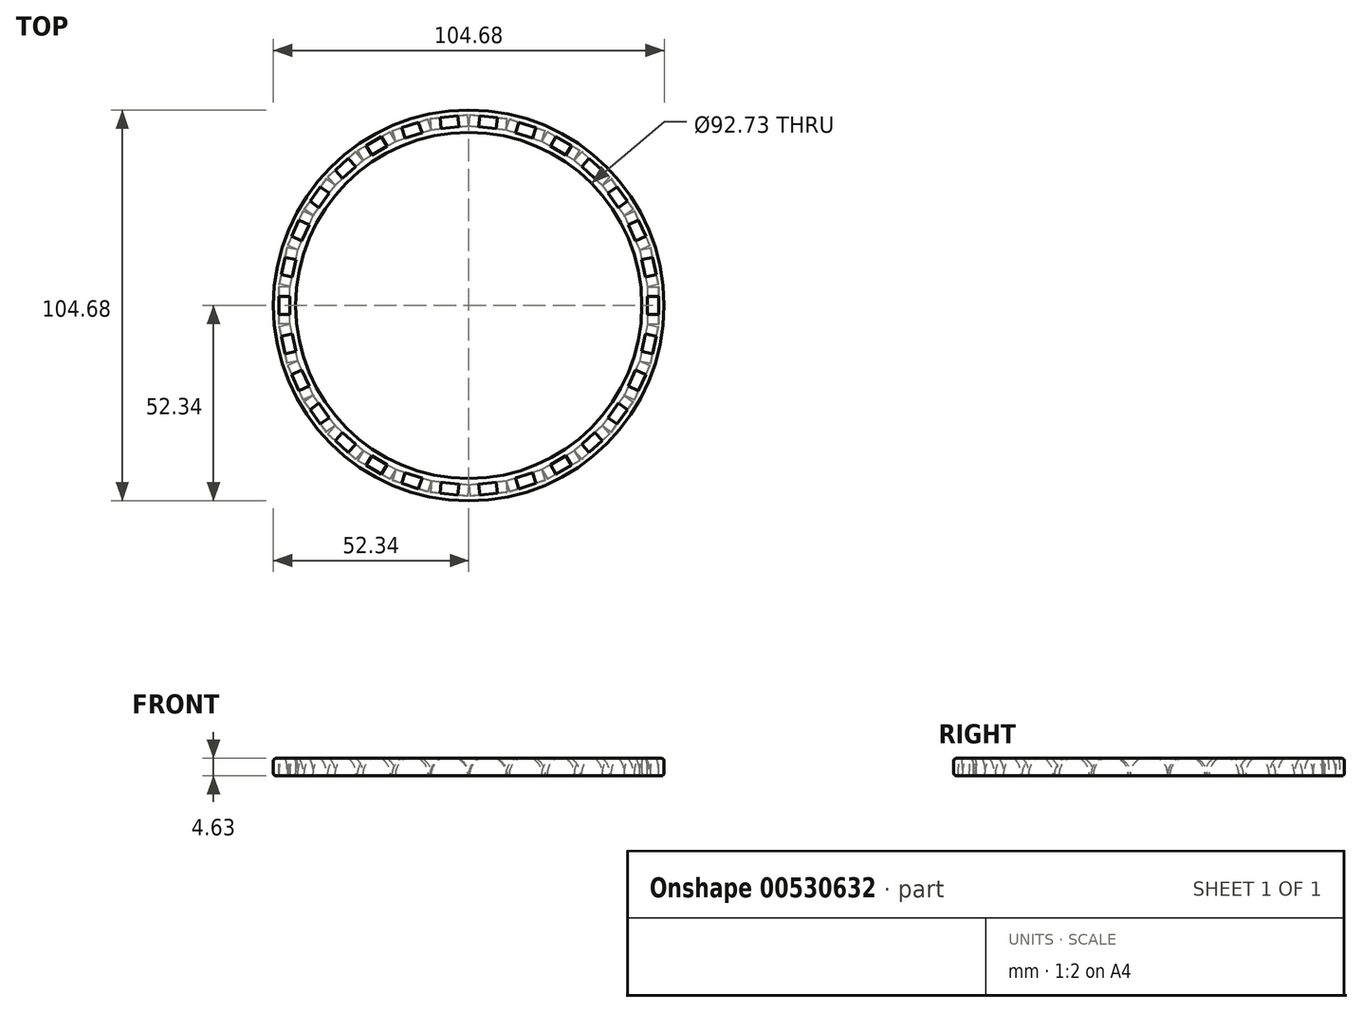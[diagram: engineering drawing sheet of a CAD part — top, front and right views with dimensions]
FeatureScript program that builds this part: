
annotation { "Feature Type Name" : "Feature", "Feature Type Description" : "" }
export const myFeature = defineFeature(function(context is Context, id is Id, definition is map)
    precondition{}
    {
        {
            var Q0;
            Q0=qCreatedBy(makeId("Front.planeOp"),FACE);
            var sketch = newSketch(context, id + "F0", { "sketchPlane" : qUnion([Q0])});
            skLineSegment(sketch, "E0", {"start": v(0, 0) * mm, "end": v(0, 19.8) * mm});
            skLineSegment(sketch, "E1", {"start": v(-50.84, 0) * mm, "end": v(-50.84, 10) * mm});
            skLineSegment(sketch, "E2", {"start": v(-50.84, 10) * mm, "end": v(-47.87, 10) * mm});
            skLineSegment(sketch, "E3", {"start": v(-47.87, 10) * mm, "end": v(-47.87, 0) * mm});
            skLineSegment(sketch, "E4", {"start": v(-47.87, 0) * mm, "end": v(-50.84, 0) * mm});
            skLineSegment(sketch, "E5", {"start": v(-50.84, 5) * mm, "end": v(-47.87, 5) * mm});
            skLineSegment(sketch, "E6", {"start": v(-50.84, 4.77) * mm, "end": v(-52.34, 4.77) * mm});
            skLineSegment(sketch, "E7", {"start": v(-52.34, 4.77) * mm, "end": v(-52.34, 9.4) * mm});
            skLineSegment(sketch, "E8", {"start": v(-52.34, 9.4) * mm, "end": v(-46.37, 9.4) * mm});
            skLineSegment(sketch, "E9", {"start": v(-46.37, 9.4) * mm, "end": v(-46.37, 4.77) * mm});
            skLineSegment(sketch, "E10", {"start": v(-46.37, 4.77) * mm, "end": v(-50.84, 4.77) * mm});
            skPoint(sketch, "E11", {"position": v(-49.35, 0) * mm});
            skSolve(sketch);
        }
        {
            var Q0;
            {var subQ3=sQuery(id+"F0.wireOp",EDGE,"E6");Q0=makeQuery(id+"F0.imprint","IMPRINT",FACE,{"disambiguationData":[TD([[makeQuery(id+"F0.imprint","IMPRINT",EDGE,{"derivedFrom":subQ3}),-1.0]])]});}
            var Q1;
            {var subQ0=sQuery(id+"F0.wireOp",EDGE,"E5");Q1=makeQuery(id+"F0.imprint","IMPRINT",FACE,{"disambiguationData":[TD([[makeQuery(id+"F0.imprint","IMPRINT",EDGE,{"derivedFrom":subQ0}),1.0]])]});}
            var Q2;
            {var subQ0=sQuery(id+"F0.wireOp",EDGE,"E9");Q2=makeQuery(id+"F0.imprint","IMPRINT",FACE,{"disambiguationData":[TD([[makeQuery(id+"F0.imprint","IMPRINT",EDGE,{"derivedFrom":subQ0}),-1.0]])]});}
            var Q3;
            {var subQ0=sQuery(id+"F0.wireOp",EDGE,"E5");Q3=makeQuery(id+"F0.imprint","IMPRINT",FACE,{"disambiguationData":[TD([[makeQuery(id+"F0.imprint","IMPRINT",EDGE,{"derivedFrom":subQ0}),-1.0]])]});}
            var Q4;
            Q4=sQuery(id+"F0.wireOp",EDGE,"E0");
            revolve(context, id + "F1", {"entities" : qUnion([Q0, Q1, Q2, Q3]), "axis" : qUnion([Q4]), "revolveType" : RevolveType.FULL});
        }
        {
            var Q0;
            {var subQ0=sQuery(id+"F0.wireOp",EDGE,"E4");Q0=makeQuery(id+"F0.imprint","IMPRINT",FACE,{"disambiguationData":[TD([[makeQuery(id+"F0.imprint","IMPRINT",EDGE,{"derivedFrom":subQ0}),-1.0]])]});}
            var Q1;
            {var subQ0=sQuery(id+"F0.wireOp",EDGE,"E5");Q1=makeQuery(id+"F0.imprint","IMPRINT",FACE,{"disambiguationData":[TD([[makeQuery(id+"F0.imprint","IMPRINT",EDGE,{"derivedFrom":subQ0}),-1.0]])]});}
            var Q2;
            Q2=sQuery(id+"F0.wireOp",EDGE,"E5");
            revolve(context, id + "F2", {"entities" : qUnion([Q0, Q1]), "axis" : qUnion([Q2]), "revolveType" : RevolveType.FULL});
        }
        {
            var Q0;
            Q0=makeQuery(id+"F2.opRevolve","SWEPT_BODY",BODY,{"disambiguationData":[OSD([sQuery(id+"F0.wireOp",EDGE,"E1"),sQuery(id+"F0.wireOp",EDGE,"E3"),sQuery(id+"F0.wireOp",EDGE,"E4"),sQuery(id+"F0.wireOp",EDGE,"E5")])]});
            var Q1;
            Q1=sQuery(id+"F0.wireOp",EDGE,"E0");
            circularPattern(context, id + "F3", {"operationType" : NewBodyOperationType.REMOVE, "entities" : qUnion([Q0]), "axis" : qUnion([Q1]), "angle" : 360 * degree, "instanceCount" : 30, "equalSpace" : true});
        }
        {
            var Q0;
            Q0=makeQuery(id+"F1.opRevolve","SWEPT_EDGE",EDGE,{"disambiguationData":[OSD([sQuery(id+"F0.wireOp",EDGE,"E6"),sQuery(id+"F0.wireOp",EDGE,"E7")])]});
            var Q1;
            Q1=makeQuery(id+"F1.opRevolve","SWEPT_EDGE",EDGE,{"disambiguationData":[OSD([sQuery(id+"F0.wireOp",EDGE,"E9"),sQuery(id+"F0.wireOp",EDGE,"E10")])]});
            var Q2;
            Q2=makeQuery(id+"F1.opRevolve","SWEPT_EDGE",EDGE,{"disambiguationData":[OSD([sQuery(id+"F0.wireOp",EDGE,"E7"),sQuery(id+"F0.wireOp",EDGE,"E8")])]});
            var Q3;
            Q3=makeQuery(id+"F1.opRevolve","SWEPT_EDGE",EDGE,{"disambiguationData":[OSD([sQuery(id+"F0.wireOp",EDGE,"E8"),sQuery(id+"F0.wireOp",EDGE,"E9")])]});
            fillet(context, id + "F4", {"entities" : qUnion([Q0, Q1, Q2, Q3]), "radius" : 0.7 * mm, "tangentPropagation" : true, "allowEdgeOverflow" : false});
        }
        {
            var Q0;
            Q0=makeQuery(id+"F3.boolean.opBoolean","INTERSECT",EDGE,{"derivedFrom":[makeQuery(id+"F1.opRevolve","SWEPT_FACE",FACE,{"disambiguationData":[OSD([sQuery(id+"F0.wireOp",EDGE,"E6"),sQuery(id+"F0.wireOp",EDGE,"E10")])]}),makeQuery(id+"F3.opPattern","COPY",FACE,{"derivedFrom":makeQuery(id+"F2.opRevolve","SWEPT_FACE",FACE,{"disambiguationData":[OSD([sQuery(id+"F0.wireOp",EDGE,"E3")])]}),"instanceName":"21"})]});
            var Q1;
            Q1=makeQuery(id+"F3.boolean.opBoolean","INTERSECT",EDGE,{"derivedFrom":[makeQuery(id+"F1.opRevolve","SWEPT_FACE",FACE,{"disambiguationData":[OSD([sQuery(id+"F0.wireOp",EDGE,"E6"),sQuery(id+"F0.wireOp",EDGE,"E10")])]}),makeQuery(id+"F3.opPattern","COPY",FACE,{"derivedFrom":makeQuery(id+"F2.opRevolve","SWEPT_FACE",FACE,{"disambiguationData":[OSD([sQuery(id+"F0.wireOp",EDGE,"E1")])]}),"instanceName":"21"})]});
            var Q2;
            Q2=makeQuery(id+"F3.boolean.opBoolean","INTERSECT",EDGE,{"derivedFrom":[makeQuery(id+"F1.opRevolve","SWEPT_FACE",FACE,{"disambiguationData":[OSD([sQuery(id+"F0.wireOp",EDGE,"E6"),sQuery(id+"F0.wireOp",EDGE,"E10")])]}),makeQuery(id+"F3.opPattern","COPY",FACE,{"derivedFrom":makeQuery(id+"F2.opRevolve","SWEPT_FACE",FACE,{"disambiguationData":[OSD([sQuery(id+"F0.wireOp",EDGE,"E1")])]}),"instanceName":"22"})]});
            var Q3;
            Q3=makeQuery(id+"F3.boolean.opBoolean","INTERSECT",EDGE,{"derivedFrom":[makeQuery(id+"F1.opRevolve","SWEPT_FACE",FACE,{"disambiguationData":[OSD([sQuery(id+"F0.wireOp",EDGE,"E6"),sQuery(id+"F0.wireOp",EDGE,"E10")])]}),makeQuery(id+"F3.opPattern","COPY",FACE,{"derivedFrom":makeQuery(id+"F2.opRevolve","SWEPT_FACE",FACE,{"disambiguationData":[OSD([sQuery(id+"F0.wireOp",EDGE,"E3")])]}),"instanceName":"22"})]});
            var Q4;
            Q4=makeQuery(id+"F3.boolean.opBoolean","INTERSECT",EDGE,{"derivedFrom":[makeQuery(id+"F1.opRevolve","SWEPT_FACE",FACE,{"disambiguationData":[OSD([sQuery(id+"F0.wireOp",EDGE,"E6"),sQuery(id+"F0.wireOp",EDGE,"E10")])]}),makeQuery(id+"F3.opPattern","COPY",FACE,{"derivedFrom":makeQuery(id+"F2.opRevolve","SWEPT_FACE",FACE,{"disambiguationData":[OSD([sQuery(id+"F0.wireOp",EDGE,"E3")])]}),"instanceName":"23"})]});
            var Q5;
            Q5=makeQuery(id+"F3.boolean.opBoolean","INTERSECT",EDGE,{"derivedFrom":[makeQuery(id+"F1.opRevolve","SWEPT_FACE",FACE,{"disambiguationData":[OSD([sQuery(id+"F0.wireOp",EDGE,"E6"),sQuery(id+"F0.wireOp",EDGE,"E10")])]}),makeQuery(id+"F3.opPattern","COPY",FACE,{"derivedFrom":makeQuery(id+"F2.opRevolve","SWEPT_FACE",FACE,{"disambiguationData":[OSD([sQuery(id+"F0.wireOp",EDGE,"E1")])]}),"instanceName":"23"})]});
            var Q6;
            Q6=makeQuery(id+"F3.boolean.opBoolean","INTERSECT",EDGE,{"derivedFrom":[makeQuery(id+"F1.opRevolve","SWEPT_FACE",FACE,{"disambiguationData":[OSD([sQuery(id+"F0.wireOp",EDGE,"E6"),sQuery(id+"F0.wireOp",EDGE,"E10")])]}),makeQuery(id+"F3.opPattern","COPY",FACE,{"derivedFrom":makeQuery(id+"F2.opRevolve","SWEPT_FACE",FACE,{"disambiguationData":[OSD([sQuery(id+"F0.wireOp",EDGE,"E1")])]}),"instanceName":"24"})]});
            var Q7;
            Q7=makeQuery(id+"F3.boolean.opBoolean","INTERSECT",EDGE,{"derivedFrom":[makeQuery(id+"F1.opRevolve","SWEPT_FACE",FACE,{"disambiguationData":[OSD([sQuery(id+"F0.wireOp",EDGE,"E6"),sQuery(id+"F0.wireOp",EDGE,"E10")])]}),makeQuery(id+"F3.opPattern","COPY",FACE,{"derivedFrom":makeQuery(id+"F2.opRevolve","SWEPT_FACE",FACE,{"disambiguationData":[OSD([sQuery(id+"F0.wireOp",EDGE,"E3")])]}),"instanceName":"24"})]});
            var Q8;
            Q8=makeQuery(id+"F3.boolean.opBoolean","INTERSECT",EDGE,{"derivedFrom":[makeQuery(id+"F1.opRevolve","SWEPT_FACE",FACE,{"disambiguationData":[OSD([sQuery(id+"F0.wireOp",EDGE,"E6"),sQuery(id+"F0.wireOp",EDGE,"E10")])]}),makeQuery(id+"F3.opPattern","COPY",FACE,{"derivedFrom":makeQuery(id+"F2.opRevolve","SWEPT_FACE",FACE,{"disambiguationData":[OSD([sQuery(id+"F0.wireOp",EDGE,"E3")])]}),"instanceName":"25"})]});
            var Q9;
            Q9=makeQuery(id+"F3.boolean.opBoolean","INTERSECT",EDGE,{"derivedFrom":[makeQuery(id+"F1.opRevolve","SWEPT_FACE",FACE,{"disambiguationData":[OSD([sQuery(id+"F0.wireOp",EDGE,"E6"),sQuery(id+"F0.wireOp",EDGE,"E10")])]}),makeQuery(id+"F3.opPattern","COPY",FACE,{"derivedFrom":makeQuery(id+"F2.opRevolve","SWEPT_FACE",FACE,{"disambiguationData":[OSD([sQuery(id+"F0.wireOp",EDGE,"E1")])]}),"instanceName":"25"})]});
            var Q10;
            Q10=makeQuery(id+"F3.boolean.opBoolean","INTERSECT",EDGE,{"derivedFrom":[makeQuery(id+"F1.opRevolve","SWEPT_FACE",FACE,{"disambiguationData":[OSD([sQuery(id+"F0.wireOp",EDGE,"E6"),sQuery(id+"F0.wireOp",EDGE,"E10")])]}),makeQuery(id+"F3.opPattern","COPY",FACE,{"derivedFrom":makeQuery(id+"F2.opRevolve","SWEPT_FACE",FACE,{"disambiguationData":[OSD([sQuery(id+"F0.wireOp",EDGE,"E1")])]}),"instanceName":"26"})]});
            var Q11;
            Q11=makeQuery(id+"F3.boolean.opBoolean","INTERSECT",EDGE,{"derivedFrom":[makeQuery(id+"F1.opRevolve","SWEPT_FACE",FACE,{"disambiguationData":[OSD([sQuery(id+"F0.wireOp",EDGE,"E6"),sQuery(id+"F0.wireOp",EDGE,"E10")])]}),makeQuery(id+"F3.opPattern","COPY",FACE,{"derivedFrom":makeQuery(id+"F2.opRevolve","SWEPT_FACE",FACE,{"disambiguationData":[OSD([sQuery(id+"F0.wireOp",EDGE,"E3")])]}),"instanceName":"26"})]});
            var Q12;
            Q12=makeQuery(id+"F3.boolean.opBoolean","INTERSECT",EDGE,{"derivedFrom":[makeQuery(id+"F1.opRevolve","SWEPT_FACE",FACE,{"disambiguationData":[OSD([sQuery(id+"F0.wireOp",EDGE,"E6"),sQuery(id+"F0.wireOp",EDGE,"E10")])]}),makeQuery(id+"F3.opPattern","COPY",FACE,{"derivedFrom":makeQuery(id+"F2.opRevolve","SWEPT_FACE",FACE,{"disambiguationData":[OSD([sQuery(id+"F0.wireOp",EDGE,"E3")])]}),"instanceName":"27"})]});
            var Q13;
            Q13=makeQuery(id+"F3.boolean.opBoolean","INTERSECT",EDGE,{"derivedFrom":[makeQuery(id+"F1.opRevolve","SWEPT_FACE",FACE,{"disambiguationData":[OSD([sQuery(id+"F0.wireOp",EDGE,"E6"),sQuery(id+"F0.wireOp",EDGE,"E10")])]}),makeQuery(id+"F3.opPattern","COPY",FACE,{"derivedFrom":makeQuery(id+"F2.opRevolve","SWEPT_FACE",FACE,{"disambiguationData":[OSD([sQuery(id+"F0.wireOp",EDGE,"E1")])]}),"instanceName":"27"})]});
            var Q14;
            Q14=makeQuery(id+"F3.boolean.opBoolean","INTERSECT",EDGE,{"derivedFrom":[makeQuery(id+"F1.opRevolve","SWEPT_FACE",FACE,{"disambiguationData":[OSD([sQuery(id+"F0.wireOp",EDGE,"E6"),sQuery(id+"F0.wireOp",EDGE,"E10")])]}),makeQuery(id+"F3.opPattern","COPY",FACE,{"derivedFrom":makeQuery(id+"F2.opRevolve","SWEPT_FACE",FACE,{"disambiguationData":[OSD([sQuery(id+"F0.wireOp",EDGE,"E1")])]}),"instanceName":"28"})]});
            var Q15;
            Q15=makeQuery(id+"F3.boolean.opBoolean","INTERSECT",EDGE,{"derivedFrom":[makeQuery(id+"F1.opRevolve","SWEPT_FACE",FACE,{"disambiguationData":[OSD([sQuery(id+"F0.wireOp",EDGE,"E6"),sQuery(id+"F0.wireOp",EDGE,"E10")])]}),makeQuery(id+"F3.opPattern","COPY",FACE,{"derivedFrom":makeQuery(id+"F2.opRevolve","SWEPT_FACE",FACE,{"disambiguationData":[OSD([sQuery(id+"F0.wireOp",EDGE,"E3")])]}),"instanceName":"28"})]});
            var Q16;
            Q16=makeQuery(id+"F3.boolean.opBoolean","INTERSECT",EDGE,{"derivedFrom":[makeQuery(id+"F1.opRevolve","SWEPT_FACE",FACE,{"disambiguationData":[OSD([sQuery(id+"F0.wireOp",EDGE,"E6"),sQuery(id+"F0.wireOp",EDGE,"E10")])]}),makeQuery(id+"F2.opRevolve","SWEPT_FACE",FACE,{"disambiguationData":[OSD([sQuery(id+"F0.wireOp",EDGE,"E1")])]})]});
            var Q17;
            Q17=makeQuery(id+"F3.boolean.opBoolean","INTERSECT",EDGE,{"derivedFrom":[makeQuery(id+"F1.opRevolve","SWEPT_FACE",FACE,{"disambiguationData":[OSD([sQuery(id+"F0.wireOp",EDGE,"E6"),sQuery(id+"F0.wireOp",EDGE,"E10")])]}),makeQuery(id+"F2.opRevolve","SWEPT_FACE",FACE,{"disambiguationData":[OSD([sQuery(id+"F0.wireOp",EDGE,"E3")])]})]});
            var Q18;
            Q18=makeQuery(id+"F3.boolean.opBoolean","INTERSECT",EDGE,{"derivedFrom":[makeQuery(id+"F1.opRevolve","SWEPT_FACE",FACE,{"disambiguationData":[OSD([sQuery(id+"F0.wireOp",EDGE,"E6"),sQuery(id+"F0.wireOp",EDGE,"E10")])]}),makeQuery(id+"F3.opPattern","COPY",FACE,{"derivedFrom":makeQuery(id+"F2.opRevolve","SWEPT_FACE",FACE,{"disambiguationData":[OSD([sQuery(id+"F0.wireOp",EDGE,"E3")])]}),"instanceName":"1"})]});
            var Q19;
            Q19=makeQuery(id+"F3.boolean.opBoolean","INTERSECT",EDGE,{"derivedFrom":[makeQuery(id+"F1.opRevolve","SWEPT_FACE",FACE,{"disambiguationData":[OSD([sQuery(id+"F0.wireOp",EDGE,"E6"),sQuery(id+"F0.wireOp",EDGE,"E10")])]}),makeQuery(id+"F3.opPattern","COPY",FACE,{"derivedFrom":makeQuery(id+"F2.opRevolve","SWEPT_FACE",FACE,{"disambiguationData":[OSD([sQuery(id+"F0.wireOp",EDGE,"E1")])]}),"instanceName":"1"})]});
            var Q20;
            Q20=makeQuery(id+"F3.boolean.opBoolean","INTERSECT",EDGE,{"derivedFrom":[makeQuery(id+"F1.opRevolve","SWEPT_FACE",FACE,{"disambiguationData":[OSD([sQuery(id+"F0.wireOp",EDGE,"E6"),sQuery(id+"F0.wireOp",EDGE,"E10")])]}),makeQuery(id+"F3.opPattern","COPY",FACE,{"derivedFrom":makeQuery(id+"F2.opRevolve","SWEPT_FACE",FACE,{"disambiguationData":[OSD([sQuery(id+"F0.wireOp",EDGE,"E3")])]}),"instanceName":"2"})]});
            var Q21;
            Q21=makeQuery(id+"F3.boolean.opBoolean","INTERSECT",EDGE,{"derivedFrom":[makeQuery(id+"F1.opRevolve","SWEPT_FACE",FACE,{"disambiguationData":[OSD([sQuery(id+"F0.wireOp",EDGE,"E6"),sQuery(id+"F0.wireOp",EDGE,"E10")])]}),makeQuery(id+"F3.opPattern","COPY",FACE,{"derivedFrom":makeQuery(id+"F2.opRevolve","SWEPT_FACE",FACE,{"disambiguationData":[OSD([sQuery(id+"F0.wireOp",EDGE,"E1")])]}),"instanceName":"2"})]});
            var Q22;
            Q22=makeQuery(id+"F3.boolean.opBoolean","INTERSECT",EDGE,{"derivedFrom":[makeQuery(id+"F1.opRevolve","SWEPT_FACE",FACE,{"disambiguationData":[OSD([sQuery(id+"F0.wireOp",EDGE,"E6"),sQuery(id+"F0.wireOp",EDGE,"E10")])]}),makeQuery(id+"F3.opPattern","COPY",FACE,{"derivedFrom":makeQuery(id+"F2.opRevolve","SWEPT_FACE",FACE,{"disambiguationData":[OSD([sQuery(id+"F0.wireOp",EDGE,"E1")])]}),"instanceName":"3"})]});
            var Q23;
            Q23=makeQuery(id+"F3.boolean.opBoolean","INTERSECT",EDGE,{"derivedFrom":[makeQuery(id+"F1.opRevolve","SWEPT_FACE",FACE,{"disambiguationData":[OSD([sQuery(id+"F0.wireOp",EDGE,"E6"),sQuery(id+"F0.wireOp",EDGE,"E10")])]}),makeQuery(id+"F3.opPattern","COPY",FACE,{"derivedFrom":makeQuery(id+"F2.opRevolve","SWEPT_FACE",FACE,{"disambiguationData":[OSD([sQuery(id+"F0.wireOp",EDGE,"E3")])]}),"instanceName":"3"})]});
            var Q24;
            Q24=makeQuery(id+"F3.boolean.opBoolean","INTERSECT",EDGE,{"derivedFrom":[makeQuery(id+"F1.opRevolve","SWEPT_FACE",FACE,{"disambiguationData":[OSD([sQuery(id+"F0.wireOp",EDGE,"E6"),sQuery(id+"F0.wireOp",EDGE,"E10")])]}),makeQuery(id+"F3.opPattern","COPY",FACE,{"derivedFrom":makeQuery(id+"F2.opRevolve","SWEPT_FACE",FACE,{"disambiguationData":[OSD([sQuery(id+"F0.wireOp",EDGE,"E3")])]}),"instanceName":"4"})]});
            var Q25;
            Q25=makeQuery(id+"F3.boolean.opBoolean","INTERSECT",EDGE,{"derivedFrom":[makeQuery(id+"F1.opRevolve","SWEPT_FACE",FACE,{"disambiguationData":[OSD([sQuery(id+"F0.wireOp",EDGE,"E6"),sQuery(id+"F0.wireOp",EDGE,"E10")])]}),makeQuery(id+"F3.opPattern","COPY",FACE,{"derivedFrom":makeQuery(id+"F2.opRevolve","SWEPT_FACE",FACE,{"disambiguationData":[OSD([sQuery(id+"F0.wireOp",EDGE,"E1")])]}),"instanceName":"4"})]});
            var Q26;
            Q26=makeQuery(id+"F3.boolean.opBoolean","INTERSECT",EDGE,{"derivedFrom":[makeQuery(id+"F1.opRevolve","SWEPT_FACE",FACE,{"disambiguationData":[OSD([sQuery(id+"F0.wireOp",EDGE,"E6"),sQuery(id+"F0.wireOp",EDGE,"E10")])]}),makeQuery(id+"F3.opPattern","COPY",FACE,{"derivedFrom":makeQuery(id+"F2.opRevolve","SWEPT_FACE",FACE,{"disambiguationData":[OSD([sQuery(id+"F0.wireOp",EDGE,"E1")])]}),"instanceName":"5"})]});
            var Q27;
            Q27=makeQuery(id+"F3.boolean.opBoolean","INTERSECT",EDGE,{"derivedFrom":[makeQuery(id+"F1.opRevolve","SWEPT_FACE",FACE,{"disambiguationData":[OSD([sQuery(id+"F0.wireOp",EDGE,"E6"),sQuery(id+"F0.wireOp",EDGE,"E10")])]}),makeQuery(id+"F3.opPattern","COPY",FACE,{"derivedFrom":makeQuery(id+"F2.opRevolve","SWEPT_FACE",FACE,{"disambiguationData":[OSD([sQuery(id+"F0.wireOp",EDGE,"E3")])]}),"instanceName":"5"})]});
            var Q28;
            Q28=makeQuery(id+"F3.boolean.opBoolean","INTERSECT",EDGE,{"derivedFrom":[makeQuery(id+"F1.opRevolve","SWEPT_FACE",FACE,{"disambiguationData":[OSD([sQuery(id+"F0.wireOp",EDGE,"E6"),sQuery(id+"F0.wireOp",EDGE,"E10")])]}),makeQuery(id+"F3.opPattern","COPY",FACE,{"derivedFrom":makeQuery(id+"F2.opRevolve","SWEPT_FACE",FACE,{"disambiguationData":[OSD([sQuery(id+"F0.wireOp",EDGE,"E1")])]}),"instanceName":"7"})]});
            var Q29;
            Q29=makeQuery(id+"F3.boolean.opBoolean","INTERSECT",EDGE,{"derivedFrom":[makeQuery(id+"F1.opRevolve","SWEPT_FACE",FACE,{"disambiguationData":[OSD([sQuery(id+"F0.wireOp",EDGE,"E6"),sQuery(id+"F0.wireOp",EDGE,"E10")])]}),makeQuery(id+"F3.opPattern","COPY",FACE,{"derivedFrom":makeQuery(id+"F2.opRevolve","SWEPT_FACE",FACE,{"disambiguationData":[OSD([sQuery(id+"F0.wireOp",EDGE,"E3")])]}),"instanceName":"7"})]});
            var Q30;
            Q30=makeQuery(id+"F3.boolean.opBoolean","INTERSECT",EDGE,{"derivedFrom":[makeQuery(id+"F1.opRevolve","SWEPT_FACE",FACE,{"disambiguationData":[OSD([sQuery(id+"F0.wireOp",EDGE,"E6"),sQuery(id+"F0.wireOp",EDGE,"E10")])]}),makeQuery(id+"F3.opPattern","COPY",FACE,{"derivedFrom":makeQuery(id+"F2.opRevolve","SWEPT_FACE",FACE,{"disambiguationData":[OSD([sQuery(id+"F0.wireOp",EDGE,"E3")])]}),"instanceName":"6"})]});
            var Q31;
            Q31=makeQuery(id+"F3.boolean.opBoolean","INTERSECT",EDGE,{"derivedFrom":[makeQuery(id+"F1.opRevolve","SWEPT_FACE",FACE,{"disambiguationData":[OSD([sQuery(id+"F0.wireOp",EDGE,"E6"),sQuery(id+"F0.wireOp",EDGE,"E10")])]}),makeQuery(id+"F3.opPattern","COPY",FACE,{"derivedFrom":makeQuery(id+"F2.opRevolve","SWEPT_FACE",FACE,{"disambiguationData":[OSD([sQuery(id+"F0.wireOp",EDGE,"E1")])]}),"instanceName":"6"})]});
            var Q32;
            Q32=makeQuery(id+"F3.boolean.opBoolean","INTERSECT",EDGE,{"derivedFrom":[makeQuery(id+"F1.opRevolve","SWEPT_FACE",FACE,{"disambiguationData":[OSD([sQuery(id+"F0.wireOp",EDGE,"E6"),sQuery(id+"F0.wireOp",EDGE,"E10")])]}),makeQuery(id+"F3.opPattern","COPY",FACE,{"derivedFrom":makeQuery(id+"F2.opRevolve","SWEPT_FACE",FACE,{"disambiguationData":[OSD([sQuery(id+"F0.wireOp",EDGE,"E1")])]}),"instanceName":"8"})]});
            var Q33;
            Q33=makeQuery(id+"F3.boolean.opBoolean","INTERSECT",EDGE,{"derivedFrom":[makeQuery(id+"F1.opRevolve","SWEPT_FACE",FACE,{"disambiguationData":[OSD([sQuery(id+"F0.wireOp",EDGE,"E6"),sQuery(id+"F0.wireOp",EDGE,"E10")])]}),makeQuery(id+"F3.opPattern","COPY",FACE,{"derivedFrom":makeQuery(id+"F2.opRevolve","SWEPT_FACE",FACE,{"disambiguationData":[OSD([sQuery(id+"F0.wireOp",EDGE,"E3")])]}),"instanceName":"8"})]});
            var Q34;
            Q34=makeQuery(id+"F3.boolean.opBoolean","INTERSECT",EDGE,{"derivedFrom":[makeQuery(id+"F1.opRevolve","SWEPT_FACE",FACE,{"disambiguationData":[OSD([sQuery(id+"F0.wireOp",EDGE,"E6"),sQuery(id+"F0.wireOp",EDGE,"E10")])]}),makeQuery(id+"F3.opPattern","COPY",FACE,{"derivedFrom":makeQuery(id+"F2.opRevolve","SWEPT_FACE",FACE,{"disambiguationData":[OSD([sQuery(id+"F0.wireOp",EDGE,"E3")])]}),"instanceName":"9"})]});
            var Q35;
            Q35=makeQuery(id+"F3.boolean.opBoolean","INTERSECT",EDGE,{"derivedFrom":[makeQuery(id+"F1.opRevolve","SWEPT_FACE",FACE,{"disambiguationData":[OSD([sQuery(id+"F0.wireOp",EDGE,"E6"),sQuery(id+"F0.wireOp",EDGE,"E10")])]}),makeQuery(id+"F3.opPattern","COPY",FACE,{"derivedFrom":makeQuery(id+"F2.opRevolve","SWEPT_FACE",FACE,{"disambiguationData":[OSD([sQuery(id+"F0.wireOp",EDGE,"E1")])]}),"instanceName":"9"})]});
            var Q36;
            Q36=makeQuery(id+"F3.boolean.opBoolean","INTERSECT",EDGE,{"derivedFrom":[makeQuery(id+"F1.opRevolve","SWEPT_FACE",FACE,{"disambiguationData":[OSD([sQuery(id+"F0.wireOp",EDGE,"E6"),sQuery(id+"F0.wireOp",EDGE,"E10")])]}),makeQuery(id+"F3.opPattern","COPY",FACE,{"derivedFrom":makeQuery(id+"F2.opRevolve","SWEPT_FACE",FACE,{"disambiguationData":[OSD([sQuery(id+"F0.wireOp",EDGE,"E3")])]}),"instanceName":"10"})]});
            var Q37;
            Q37=makeQuery(id+"F3.boolean.opBoolean","INTERSECT",EDGE,{"derivedFrom":[makeQuery(id+"F1.opRevolve","SWEPT_FACE",FACE,{"disambiguationData":[OSD([sQuery(id+"F0.wireOp",EDGE,"E6"),sQuery(id+"F0.wireOp",EDGE,"E10")])]}),makeQuery(id+"F3.opPattern","COPY",FACE,{"derivedFrom":makeQuery(id+"F2.opRevolve","SWEPT_FACE",FACE,{"disambiguationData":[OSD([sQuery(id+"F0.wireOp",EDGE,"E1")])]}),"instanceName":"10"})]});
            var Q38;
            Q38=makeQuery(id+"F3.boolean.opBoolean","INTERSECT",EDGE,{"derivedFrom":[makeQuery(id+"F1.opRevolve","SWEPT_FACE",FACE,{"disambiguationData":[OSD([sQuery(id+"F0.wireOp",EDGE,"E6"),sQuery(id+"F0.wireOp",EDGE,"E10")])]}),makeQuery(id+"F3.opPattern","COPY",FACE,{"derivedFrom":makeQuery(id+"F2.opRevolve","SWEPT_FACE",FACE,{"disambiguationData":[OSD([sQuery(id+"F0.wireOp",EDGE,"E1")])]}),"instanceName":"11"})]});
            var Q39;
            Q39=makeQuery(id+"F3.boolean.opBoolean","INTERSECT",EDGE,{"derivedFrom":[makeQuery(id+"F1.opRevolve","SWEPT_FACE",FACE,{"disambiguationData":[OSD([sQuery(id+"F0.wireOp",EDGE,"E6"),sQuery(id+"F0.wireOp",EDGE,"E10")])]}),makeQuery(id+"F3.opPattern","COPY",FACE,{"derivedFrom":makeQuery(id+"F2.opRevolve","SWEPT_FACE",FACE,{"disambiguationData":[OSD([sQuery(id+"F0.wireOp",EDGE,"E3")])]}),"instanceName":"11"})]});
            var Q40;
            Q40=makeQuery(id+"F3.boolean.opBoolean","INTERSECT",EDGE,{"derivedFrom":[makeQuery(id+"F1.opRevolve","SWEPT_FACE",FACE,{"disambiguationData":[OSD([sQuery(id+"F0.wireOp",EDGE,"E6"),sQuery(id+"F0.wireOp",EDGE,"E10")])]}),makeQuery(id+"F3.opPattern","COPY",FACE,{"derivedFrom":makeQuery(id+"F2.opRevolve","SWEPT_FACE",FACE,{"disambiguationData":[OSD([sQuery(id+"F0.wireOp",EDGE,"E3")])]}),"instanceName":"12"})]});
            var Q41;
            Q41=makeQuery(id+"F3.boolean.opBoolean","INTERSECT",EDGE,{"derivedFrom":[makeQuery(id+"F1.opRevolve","SWEPT_FACE",FACE,{"disambiguationData":[OSD([sQuery(id+"F0.wireOp",EDGE,"E6"),sQuery(id+"F0.wireOp",EDGE,"E10")])]}),makeQuery(id+"F3.opPattern","COPY",FACE,{"derivedFrom":makeQuery(id+"F2.opRevolve","SWEPT_FACE",FACE,{"disambiguationData":[OSD([sQuery(id+"F0.wireOp",EDGE,"E1")])]}),"instanceName":"13"})]});
            var Q42;
            Q42=makeQuery(id+"F3.boolean.opBoolean","INTERSECT",EDGE,{"derivedFrom":[makeQuery(id+"F1.opRevolve","SWEPT_FACE",FACE,{"disambiguationData":[OSD([sQuery(id+"F0.wireOp",EDGE,"E6"),sQuery(id+"F0.wireOp",EDGE,"E10")])]}),makeQuery(id+"F3.opPattern","COPY",FACE,{"derivedFrom":makeQuery(id+"F2.opRevolve","SWEPT_FACE",FACE,{"disambiguationData":[OSD([sQuery(id+"F0.wireOp",EDGE,"E3")])]}),"instanceName":"13"})]});
            var Q43;
            Q43=makeQuery(id+"F3.boolean.opBoolean","INTERSECT",EDGE,{"derivedFrom":[makeQuery(id+"F1.opRevolve","SWEPT_FACE",FACE,{"disambiguationData":[OSD([sQuery(id+"F0.wireOp",EDGE,"E6"),sQuery(id+"F0.wireOp",EDGE,"E10")])]}),makeQuery(id+"F3.opPattern","COPY",FACE,{"derivedFrom":makeQuery(id+"F2.opRevolve","SWEPT_FACE",FACE,{"disambiguationData":[OSD([sQuery(id+"F0.wireOp",EDGE,"E3")])]}),"instanceName":"14"})]});
            var Q44;
            Q44=makeQuery(id+"F3.boolean.opBoolean","INTERSECT",EDGE,{"derivedFrom":[makeQuery(id+"F1.opRevolve","SWEPT_FACE",FACE,{"disambiguationData":[OSD([sQuery(id+"F0.wireOp",EDGE,"E6"),sQuery(id+"F0.wireOp",EDGE,"E10")])]}),makeQuery(id+"F3.opPattern","COPY",FACE,{"derivedFrom":makeQuery(id+"F2.opRevolve","SWEPT_FACE",FACE,{"disambiguationData":[OSD([sQuery(id+"F0.wireOp",EDGE,"E1")])]}),"instanceName":"14"})]});
            var Q45;
            Q45=makeQuery(id+"F3.boolean.opBoolean","INTERSECT",EDGE,{"derivedFrom":[makeQuery(id+"F1.opRevolve","SWEPT_FACE",FACE,{"disambiguationData":[OSD([sQuery(id+"F0.wireOp",EDGE,"E6"),sQuery(id+"F0.wireOp",EDGE,"E10")])]}),makeQuery(id+"F3.opPattern","COPY",FACE,{"derivedFrom":makeQuery(id+"F2.opRevolve","SWEPT_FACE",FACE,{"disambiguationData":[OSD([sQuery(id+"F0.wireOp",EDGE,"E1")])]}),"instanceName":"12"})]});
            var Q46;
            Q46=makeQuery(id+"F3.boolean.opBoolean","INTERSECT",EDGE,{"derivedFrom":[makeQuery(id+"F1.opRevolve","SWEPT_FACE",FACE,{"disambiguationData":[OSD([sQuery(id+"F0.wireOp",EDGE,"E6"),sQuery(id+"F0.wireOp",EDGE,"E10")])]}),makeQuery(id+"F3.opPattern","COPY",FACE,{"derivedFrom":makeQuery(id+"F2.opRevolve","SWEPT_FACE",FACE,{"disambiguationData":[OSD([sQuery(id+"F0.wireOp",EDGE,"E3")])]}),"instanceName":"15"})]});
            var Q47;
            Q47=makeQuery(id+"F3.boolean.opBoolean","INTERSECT",EDGE,{"derivedFrom":[makeQuery(id+"F1.opRevolve","SWEPT_FACE",FACE,{"disambiguationData":[OSD([sQuery(id+"F0.wireOp",EDGE,"E6"),sQuery(id+"F0.wireOp",EDGE,"E10")])]}),makeQuery(id+"F3.opPattern","COPY",FACE,{"derivedFrom":makeQuery(id+"F2.opRevolve","SWEPT_FACE",FACE,{"disambiguationData":[OSD([sQuery(id+"F0.wireOp",EDGE,"E3")])]}),"instanceName":"16"})]});
            var Q48;
            Q48=makeQuery(id+"F3.boolean.opBoolean","INTERSECT",EDGE,{"derivedFrom":[makeQuery(id+"F1.opRevolve","SWEPT_FACE",FACE,{"disambiguationData":[OSD([sQuery(id+"F0.wireOp",EDGE,"E6"),sQuery(id+"F0.wireOp",EDGE,"E10")])]}),makeQuery(id+"F3.opPattern","COPY",FACE,{"derivedFrom":makeQuery(id+"F2.opRevolve","SWEPT_FACE",FACE,{"disambiguationData":[OSD([sQuery(id+"F0.wireOp",EDGE,"E3")])]}),"instanceName":"17"})]});
            var Q49;
            Q49=makeQuery(id+"F3.boolean.opBoolean","INTERSECT",EDGE,{"derivedFrom":[makeQuery(id+"F1.opRevolve","SWEPT_FACE",FACE,{"disambiguationData":[OSD([sQuery(id+"F0.wireOp",EDGE,"E6"),sQuery(id+"F0.wireOp",EDGE,"E10")])]}),makeQuery(id+"F3.opPattern","COPY",FACE,{"derivedFrom":makeQuery(id+"F2.opRevolve","SWEPT_FACE",FACE,{"disambiguationData":[OSD([sQuery(id+"F0.wireOp",EDGE,"E3")])]}),"instanceName":"18"})]});
            var Q50;
            Q50=makeQuery(id+"F3.boolean.opBoolean","INTERSECT",EDGE,{"derivedFrom":[makeQuery(id+"F1.opRevolve","SWEPT_FACE",FACE,{"disambiguationData":[OSD([sQuery(id+"F0.wireOp",EDGE,"E6"),sQuery(id+"F0.wireOp",EDGE,"E10")])]}),makeQuery(id+"F3.opPattern","COPY",FACE,{"derivedFrom":makeQuery(id+"F2.opRevolve","SWEPT_FACE",FACE,{"disambiguationData":[OSD([sQuery(id+"F0.wireOp",EDGE,"E3")])]}),"instanceName":"19"})]});
            var Q51;
            Q51=makeQuery(id+"F3.boolean.opBoolean","INTERSECT",EDGE,{"derivedFrom":[makeQuery(id+"F1.opRevolve","SWEPT_FACE",FACE,{"disambiguationData":[OSD([sQuery(id+"F0.wireOp",EDGE,"E6"),sQuery(id+"F0.wireOp",EDGE,"E10")])]}),makeQuery(id+"F3.opPattern","COPY",FACE,{"derivedFrom":makeQuery(id+"F2.opRevolve","SWEPT_FACE",FACE,{"disambiguationData":[OSD([sQuery(id+"F0.wireOp",EDGE,"E3")])]}),"instanceName":"20"})]});
            var Q52;
            Q52=makeQuery(id+"F3.boolean.opBoolean","INTERSECT",EDGE,{"derivedFrom":[makeQuery(id+"F1.opRevolve","SWEPT_FACE",FACE,{"disambiguationData":[OSD([sQuery(id+"F0.wireOp",EDGE,"E6"),sQuery(id+"F0.wireOp",EDGE,"E10")])]}),makeQuery(id+"F3.opPattern","COPY",FACE,{"derivedFrom":makeQuery(id+"F2.opRevolve","SWEPT_FACE",FACE,{"disambiguationData":[OSD([sQuery(id+"F0.wireOp",EDGE,"E1")])]}),"instanceName":"20"})]});
            var Q53;
            Q53=makeQuery(id+"F3.boolean.opBoolean","INTERSECT",EDGE,{"derivedFrom":[makeQuery(id+"F1.opRevolve","SWEPT_FACE",FACE,{"disambiguationData":[OSD([sQuery(id+"F0.wireOp",EDGE,"E6"),sQuery(id+"F0.wireOp",EDGE,"E10")])]}),makeQuery(id+"F3.opPattern","COPY",FACE,{"derivedFrom":makeQuery(id+"F2.opRevolve","SWEPT_FACE",FACE,{"disambiguationData":[OSD([sQuery(id+"F0.wireOp",EDGE,"E1")])]}),"instanceName":"19"})]});
            var Q54;
            Q54=makeQuery(id+"F3.boolean.opBoolean","INTERSECT",EDGE,{"derivedFrom":[makeQuery(id+"F1.opRevolve","SWEPT_FACE",FACE,{"disambiguationData":[OSD([sQuery(id+"F0.wireOp",EDGE,"E6"),sQuery(id+"F0.wireOp",EDGE,"E10")])]}),makeQuery(id+"F3.opPattern","COPY",FACE,{"derivedFrom":makeQuery(id+"F2.opRevolve","SWEPT_FACE",FACE,{"disambiguationData":[OSD([sQuery(id+"F0.wireOp",EDGE,"E1")])]}),"instanceName":"18"})]});
            var Q55;
            Q55=makeQuery(id+"F3.boolean.opBoolean","INTERSECT",EDGE,{"derivedFrom":[makeQuery(id+"F1.opRevolve","SWEPT_FACE",FACE,{"disambiguationData":[OSD([sQuery(id+"F0.wireOp",EDGE,"E6"),sQuery(id+"F0.wireOp",EDGE,"E10")])]}),makeQuery(id+"F3.opPattern","COPY",FACE,{"derivedFrom":makeQuery(id+"F2.opRevolve","SWEPT_FACE",FACE,{"disambiguationData":[OSD([sQuery(id+"F0.wireOp",EDGE,"E1")])]}),"instanceName":"17"})]});
            var Q56;
            Q56=makeQuery(id+"F3.boolean.opBoolean","INTERSECT",EDGE,{"derivedFrom":[makeQuery(id+"F1.opRevolve","SWEPT_FACE",FACE,{"disambiguationData":[OSD([sQuery(id+"F0.wireOp",EDGE,"E6"),sQuery(id+"F0.wireOp",EDGE,"E10")])]}),makeQuery(id+"F3.opPattern","COPY",FACE,{"derivedFrom":makeQuery(id+"F2.opRevolve","SWEPT_FACE",FACE,{"disambiguationData":[OSD([sQuery(id+"F0.wireOp",EDGE,"E1")])]}),"instanceName":"16"})]});
            var Q57;
            Q57=makeQuery(id+"F3.boolean.opBoolean","INTERSECT",EDGE,{"derivedFrom":[makeQuery(id+"F1.opRevolve","SWEPT_FACE",FACE,{"disambiguationData":[OSD([sQuery(id+"F0.wireOp",EDGE,"E6"),sQuery(id+"F0.wireOp",EDGE,"E10")])]}),makeQuery(id+"F3.opPattern","COPY",FACE,{"derivedFrom":makeQuery(id+"F2.opRevolve","SWEPT_FACE",FACE,{"disambiguationData":[OSD([sQuery(id+"F0.wireOp",EDGE,"E1")])]}),"instanceName":"16"})]});
            var Q58;
            Q58=makeQuery(id+"F3.boolean.opBoolean","INTERSECT",EDGE,{"derivedFrom":[makeQuery(id+"F1.opRevolve","SWEPT_FACE",FACE,{"disambiguationData":[OSD([sQuery(id+"F0.wireOp",EDGE,"E6"),sQuery(id+"F0.wireOp",EDGE,"E10")])]}),makeQuery(id+"F3.opPattern","COPY",FACE,{"derivedFrom":makeQuery(id+"F2.opRevolve","SWEPT_FACE",FACE,{"disambiguationData":[OSD([sQuery(id+"F0.wireOp",EDGE,"E1")])]}),"instanceName":"15"})]});
            var Q59;
            Q59=makeQuery(id+"F3.boolean.opBoolean","INTERSECT",EDGE,{"derivedFrom":[makeQuery(id+"F1.opRevolve","SWEPT_FACE",FACE,{"disambiguationData":[OSD([sQuery(id+"F0.wireOp",EDGE,"E6"),sQuery(id+"F0.wireOp",EDGE,"E10")])]}),makeQuery(id+"F3.opPattern","COPY",FACE,{"derivedFrom":makeQuery(id+"F2.opRevolve","SWEPT_FACE",FACE,{"disambiguationData":[OSD([sQuery(id+"F0.wireOp",EDGE,"E1")])]}),"instanceName":"29"})]});
            var Q60;
            Q60=makeQuery(id+"F3.boolean.opBoolean","INTERSECT",EDGE,{"derivedFrom":[makeQuery(id+"F1.opRevolve","SWEPT_FACE",FACE,{"disambiguationData":[OSD([sQuery(id+"F0.wireOp",EDGE,"E6"),sQuery(id+"F0.wireOp",EDGE,"E10")])]}),makeQuery(id+"F3.opPattern","COPY",FACE,{"derivedFrom":makeQuery(id+"F2.opRevolve","SWEPT_FACE",FACE,{"disambiguationData":[OSD([sQuery(id+"F0.wireOp",EDGE,"E3")])]}),"instanceName":"29"})]});
            fillet(context, id + "F5", {"entities" : qUnion([Q0, Q1, Q2, Q3, Q4, Q5, Q6, Q7, Q8, Q9, Q10, Q11, Q12, Q13, Q14, Q15, Q16, Q17, Q18, Q19, Q20, Q21, Q22, Q23, Q24, Q25, Q26, Q27, Q28, Q29, Q30, Q31, Q32, Q33, Q34, Q35, Q36, Q37, Q38, Q39, Q40, Q41, Q42, Q43, Q44, Q45, Q46, Q47, Q48, Q49, Q50, Q51, Q52, Q53, Q54, Q55, Q56, Q57, Q58, Q59, Q60]), "radius" : 0.16 * mm, "tangentPropagation" : true, "allowEdgeOverflow" : false});
        }
    });
